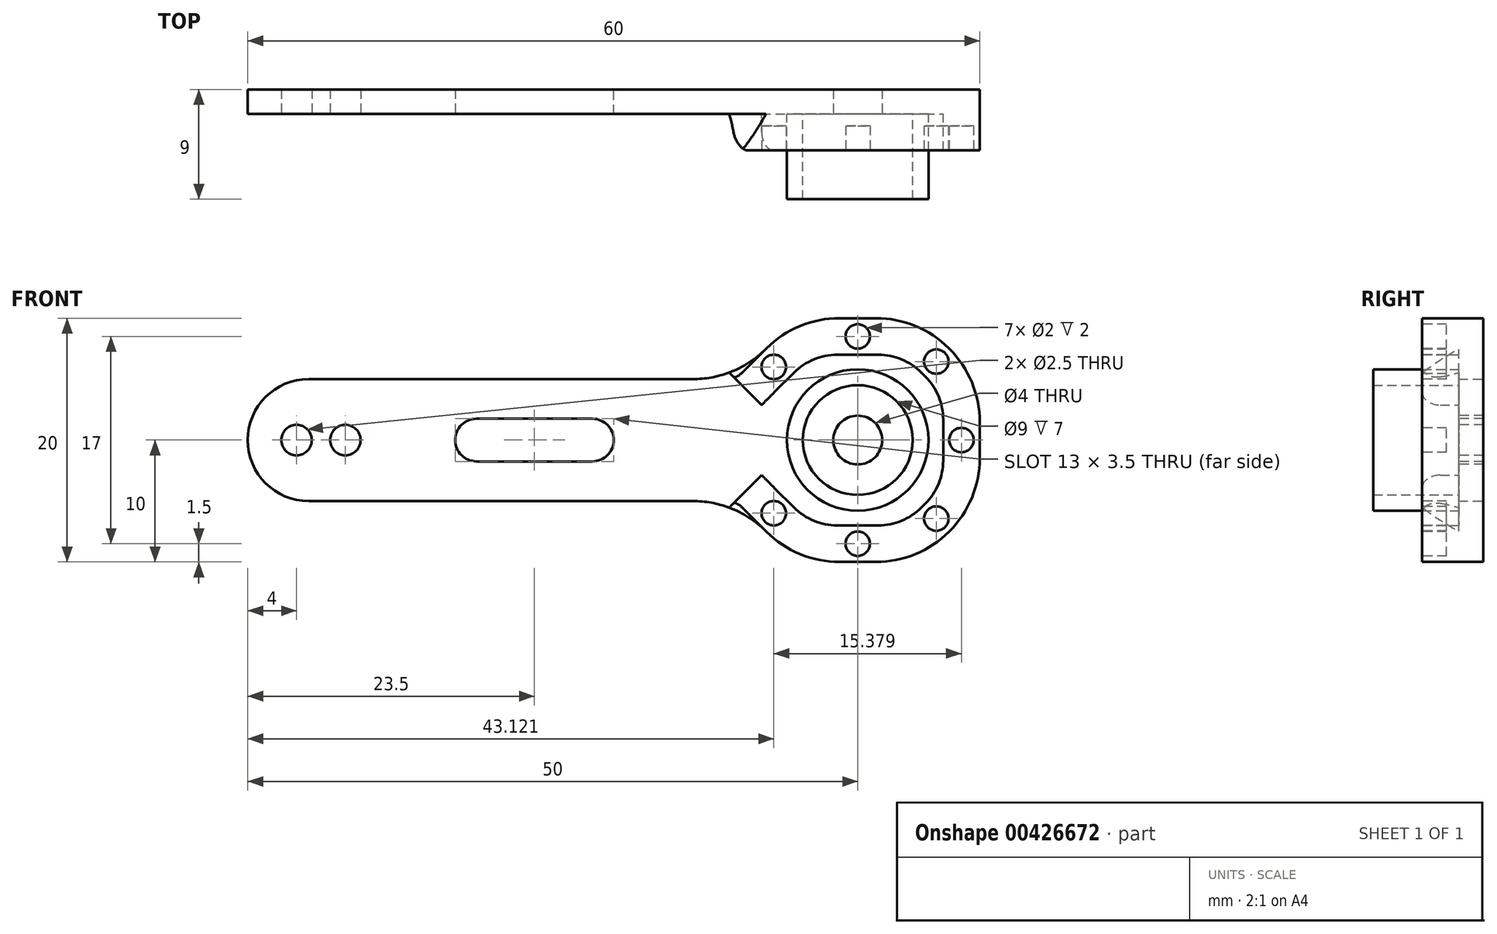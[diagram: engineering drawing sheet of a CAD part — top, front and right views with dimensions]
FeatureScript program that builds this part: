
annotation { "Feature Type Name" : "Feature", "Feature Type Description" : "" }
export const myFeature = defineFeature(function(context is Context, id is Id, definition is map)
    precondition{}
    {
        {
            var Q0;
            Q0=qCreatedBy(makeId("Front.planeOp"),FACE);
            var sketch = newSketch(context, id + "F0", { "sketchPlane" : qUnion([Q0])});
            skLineSegment(sketch, "E0", {"start": v(0, 0) * mm, "end": v(40, 0) * mm});
            skLineSegment(sketch, "E1", {"start": v(60, 0) * mm, "end": v(60, 10) * mm});
            skLineSegment(sketch, "E2", {"start": v(40, 10) * mm, "end": v(0, 10) * mm});
            skLineSegment(sketch, "E3", {"start": v(0, 10) * mm, "end": v(0, 0) * mm});
            skLineSegment(sketch, "E4", {"start": v(40, 10) * mm, "end": v(45, 15) * mm});
            skLineSegment(sketch, "E5", {"start": v(45, 15) * mm, "end": v(55, 15) * mm});
            skLineSegment(sketch, "E6", {"start": v(55, 15) * mm, "end": v(60, 10) * mm});
            skLineSegment(sketch, "E7", {"start": v(40, 0) * mm, "end": v(45, -5) * mm});
            skLineSegment(sketch, "E8", {"start": v(45, -5) * mm, "end": v(55, -5) * mm});
            skLineSegment(sketch, "E9", {"start": v(55, -5) * mm, "end": v(60, 0) * mm});
            skSolve(sketch);
        }
        {
            var Q0;
            Q0 = qSketchRegion(id + "F0", true);
            extrude(context, id + "F1", {"entities" : qUnion([Q0]), "depth" : 2 * mm, "offsetDistance" : 25 * mm});
        }
        {
            var Q0;
            Q0=makeQuery(id+"F1.opExtrude","CAP_FACE",FACE,{"disambiguationData":[OSD([sQuery(id+"F0.wireOp",EDGE,"E0"),sQuery(id+"F0.wireOp",EDGE,"E1"),sQuery(id+"F0.wireOp",EDGE,"E2"),sQuery(id+"F0.wireOp",EDGE,"E3"),sQuery(id+"F0.wireOp",EDGE,"E4"),sQuery(id+"F0.wireOp",EDGE,"E5"),sQuery(id+"F0.wireOp",EDGE,"E6"),sQuery(id+"F0.wireOp",EDGE,"E7"),sQuery(id+"F0.wireOp",EDGE,"E8"),sQuery(id+"F0.wireOp",EDGE,"E9")])],"isStart":false});
            var sketch = newSketch(context, id + "F2", { "sketchPlane" : qUnion([Q0])});
            skCircle(sketch, "E10", {"center": v(4, 5) * mm, "radius": 1.25 * mm});
            skCircle(sketch, "E11", {"center": v(8, 5) * mm, "radius": 1.25 * mm});
            skSolve(sketch);
        }
        {
            var Q0;
            Q0 = qSketchRegion(id + "F2", true);
            extrude(context, id + "F3", {"entities" : qUnion([Q0]), "operationType" : NewBodyOperationType.REMOVE, "oppositeDirection" : true, "depth" : 25 * mm, "offsetDistance" : 25 * mm});
        }
        {
            var Q0;
            Q0=makeQuery(id+"F1.opExtrude","CAP_FACE",FACE,{"disambiguationData":[OSD([sQuery(id+"F0.wireOp",EDGE,"E0"),sQuery(id+"F0.wireOp",EDGE,"E1"),sQuery(id+"F0.wireOp",EDGE,"E2"),sQuery(id+"F0.wireOp",EDGE,"E3"),sQuery(id+"F0.wireOp",EDGE,"E4"),sQuery(id+"F0.wireOp",EDGE,"E5"),sQuery(id+"F0.wireOp",EDGE,"E6"),sQuery(id+"F0.wireOp",EDGE,"E7"),sQuery(id+"F0.wireOp",EDGE,"E8"),sQuery(id+"F0.wireOp",EDGE,"E9")])],"isStart":false});
            var sketch = newSketch(context, id + "F4", { "sketchPlane" : qUnion([Q0])});
            skCircle(sketch, "E12", {"center": v(50, 5) * mm, "radius": 2 * mm});
            skSolve(sketch);
        }
        {
            var Q0;
            Q0 = qSketchRegion(id + "F4", true);
            extrude(context, id + "F5", {"entities" : qUnion([Q0]), "operationType" : NewBodyOperationType.REMOVE, "oppositeDirection" : true, "depth" : 25 * mm, "offsetDistance" : 25 * mm});
        }
        {
            var Q0;
            Q0=makeQuery(id+"F1.opExtrude","CAP_FACE",FACE,{"disambiguationData":[OSD([sQuery(id+"F0.wireOp",EDGE,"E0"),sQuery(id+"F0.wireOp",EDGE,"E1"),sQuery(id+"F0.wireOp",EDGE,"E2"),sQuery(id+"F0.wireOp",EDGE,"E3"),sQuery(id+"F0.wireOp",EDGE,"E4"),sQuery(id+"F0.wireOp",EDGE,"E5"),sQuery(id+"F0.wireOp",EDGE,"E6"),sQuery(id+"F0.wireOp",EDGE,"E7"),sQuery(id+"F0.wireOp",EDGE,"E8"),sQuery(id+"F0.wireOp",EDGE,"E9")])],"isStart":false});
            var sketch = newSketch(context, id + "F6", { "sketchPlane" : qUnion([Q0])});
            skCircle(sketch, "E13", {"center": v(50, 5) * mm, "radius": 4.5 * mm});
            skCircle(sketch, "E14", {"center": v(50, 5) * mm, "radius": 5.8 * mm});
            skSolve(sketch);
        }
        {
            var Q0;
            Q0 = qSketchRegion(id + "F6", true);
            extrude(context, id + "F7", {"entities" : qUnion([Q0]), "operationType" : NewBodyOperationType.ADD, "depth" : 7 * mm, "offsetDistance" : 25 * mm});
        }
        {
            var Q0;
            {var subQ0=sQuery(id+"F0.wireOp",EDGE,"E8");var subQ1=sQuery(id+"F0.wireOp",EDGE,"E7");var subQ2=sQuery(id+"F0.wireOp",EDGE,"E6");var subQ3=sQuery(id+"F0.wireOp",EDGE,"E5");var subQ4=sQuery(id+"F0.wireOp",EDGE,"E4");var subQ5=sQuery(id+"F0.wireOp",EDGE,"E9");var subQ6=sQuery(id+"F0.wireOp",EDGE,"E0");var subQ7=sQuery(id+"F0.wireOp",EDGE,"E3");var subQ8=sQuery(id+"F0.wireOp",EDGE,"E1");var subQ9=sQuery(id+"F0.wireOp",EDGE,"E2");Q0=makeQuery(id+"F7.boolean.opBoolean","SPLIT",FACE,{"disambiguationData":[TD([makeQuery(id+"F1.opExtrude","SWEPT_FACE",FACE,{"disambiguationData":[OSD([subQ6])]})])],"derivedFrom":makeQuery(id+"F1.opExtrude","CAP_FACE",FACE,{"disambiguationData":[OSD([subQ6,subQ8,subQ9,subQ7,subQ4,subQ3,subQ2,subQ1,subQ0,subQ5])],"isStart":false})});}
            var sketch = newSketch(context, id + "F8", { "sketchPlane" : qUnion([Q0])});
            skLineSegment(sketch, "E15", {"start": v(40, 0) * mm, "end": v(45, -5) * mm});
            skLineSegment(sketch, "E16", {"start": v(45, -5) * mm, "end": v(55, -5) * mm});
            skLineSegment(sketch, "E17", {"start": v(55, -5) * mm, "end": v(60, 0) * mm});
            skLineSegment(sketch, "E18", {"start": v(60, 0) * mm, "end": v(60, 10) * mm});
            skLineSegment(sketch, "E19", {"start": v(60, 10) * mm, "end": v(55, 15) * mm});
            skLineSegment(sketch, "E20", {"start": v(55, 15) * mm, "end": v(45, 15) * mm});
            skLineSegment(sketch, "E21", {"start": v(45, 15) * mm, "end": v(40, 10) * mm});
            skLineSegment(sketch, "E22.0", {"start": v(46.24, 12) * mm, "end": v(42.12, 7.88) * mm});
            skLineSegment(sketch, "E22.1", {"start": v(53.76, 12) * mm, "end": v(46.24, 12) * mm});
            skLineSegment(sketch, "E22.2", {"start": v(57, 8.76) * mm, "end": v(53.76, 12) * mm});
            skLineSegment(sketch, "E22.3", {"start": v(42.12, 2.12) * mm, "end": v(46.24, -2) * mm});
            skLineSegment(sketch, "E22.4", {"start": v(46.24, -2) * mm, "end": v(53.76, -2) * mm});
            skLineSegment(sketch, "E22.5", {"start": v(53.76, -2) * mm, "end": v(57, 1.24) * mm});
            skLineSegment(sketch, "E22.6", {"start": v(57, 1.24) * mm, "end": v(57, 8.76) * mm});
            skLineSegment(sketch, "E23", {"start": v(42.12, 7.88) * mm, "end": v(40, 10) * mm});
            skLineSegment(sketch, "E24", {"start": v(42.12, 2.12) * mm, "end": v(40, 0) * mm});
            skLineSegment(sketch, "E25", {"start": v(53.76, 12) * mm, "end": v(55, 15) * mm});
            skLineSegment(sketch, "E26", {"start": v(53.76, -2) * mm, "end": v(55, -5) * mm});
            skSolve(sketch);
        }
        {
            var Q0;
            Q0 = qSketchRegion(id + "F8", true);
            extrude(context, id + "F9", {"entities" : qUnion([Q0]), "operationType" : NewBodyOperationType.ADD, "depth" : 3 * mm, "offsetDistance" : 25 * mm});
        }
        {
            var Q0;
            Q0=makeQuery(id+"F9.opExtrude","CAP_FACE",FACE,{"disambiguationData":[OSD([sQuery(id+"F8.wireOp",EDGE,"E15"),sQuery(id+"F8.wireOp",EDGE,"E16"),sQuery(id+"F8.wireOp",EDGE,"E17"),sQuery(id+"F8.wireOp",EDGE,"E18"),sQuery(id+"F8.wireOp",EDGE,"E19"),sQuery(id+"F8.wireOp",EDGE,"E20"),sQuery(id+"F8.wireOp",EDGE,"E21"),sQuery(id+"F8.wireOp",EDGE,"E22.0"),sQuery(id+"F8.wireOp",EDGE,"E22.1"),sQuery(id+"F8.wireOp",EDGE,"E22.2"),sQuery(id+"F8.wireOp",EDGE,"E22.3"),sQuery(id+"F8.wireOp",EDGE,"E22.4"),sQuery(id+"F8.wireOp",EDGE,"E22.5"),sQuery(id+"F8.wireOp",EDGE,"E22.6"),sQuery(id+"F8.wireOp",EDGE,"E23"),sQuery(id+"F8.wireOp",EDGE,"E24")])],"isStart":false});
            var sketch = newSketch(context, id + "F10", { "sketchPlane" : qUnion([Q0])});
            skCircle(sketch, "E27", {"center": v(50, -3.5) * mm, "radius": 1 * mm});
            skCircle(sketch, "E28", {"center": v(58.5, 5) * mm, "radius": 1 * mm});
            skPoint(sketch, "E28.centerSnap0", {"position": v(57, 5) * mm});
            skCircle(sketch, "E29", {"center": v(56.44, 11.44) * mm, "radius": 1 * mm});
            skCircle(sketch, "E30", {"center": v(50, 13.5) * mm, "radius": 1 * mm});
            skCircle(sketch, "E31", {"center": v(43.12, 11) * mm, "radius": 1 * mm});
            skCircle(sketch, "E32", {"center": v(43.12, -1) * mm, "radius": 1 * mm});
            skPoint(sketch, "E33.start.orphan", {"position": v(44.18, 0.06) * mm});
            skPoint(sketch, "E34.orphan", {"position": v(44.18, 9.94) * mm});
            skPoint(sketch, "E35.orphan", {"position": v(55.38, 10.38) * mm});
            skPoint(sketch, "E36.end.orphan", {"position": v(57.5, 12.5) * mm});
            skCircle(sketch, "E37", {"center": v(56.44, -1.44) * mm, "radius": 1 * mm});
            skPoint(sketch, "E38.orphan", {"position": v(57.5, -2.5) * mm});
            skPoint(sketch, "E39.orphan", {"position": v(55.38, -0.38) * mm});
            skSolve(sketch);
        }
        {
            var Q0;
            Q0 = qSketchRegion(id + "F10", true);
            extrude(context, id + "F11", {"entities" : qUnion([Q0]), "operationType" : NewBodyOperationType.REMOVE, "oppositeDirection" : true, "depth" : 2 * mm, "offsetDistance" : 25 * mm});
        }
        {
            var Q0;
            Q0=makeQuery(id+"F1.opExtrude","SWEPT_EDGE",EDGE,{"disambiguationData":[OSD([sQuery(id+"F0.wireOp",EDGE,"E2"),sQuery(id+"F0.wireOp",EDGE,"E4")])]});
            var Q1;
            Q1=makeQuery(id+"F9.boolean.opBoolean","MERGE",EDGE,{"derivedFrom":[makeQuery(id+"F1.opExtrude","SWEPT_EDGE",EDGE,{"disambiguationData":[OSD([sQuery(id+"F0.wireOp",EDGE,"E4"),sQuery(id+"F0.wireOp",EDGE,"E5")])]}),makeQuery(id+"F9.opExtrude","SWEPT_EDGE",EDGE,{"disambiguationData":[OSD([sQuery(id+"F8.wireOp",EDGE,"E20"),sQuery(id+"F8.wireOp",EDGE,"E21")])]})]});
            var Q2;
            Q2=makeQuery(id+"F9.boolean.opBoolean","MERGE",EDGE,{"derivedFrom":[makeQuery(id+"F1.opExtrude","SWEPT_EDGE",EDGE,{"disambiguationData":[OSD([sQuery(id+"F0.wireOp",EDGE,"E5"),sQuery(id+"F0.wireOp",EDGE,"E6")])]}),makeQuery(id+"F9.opExtrude","SWEPT_EDGE",EDGE,{"disambiguationData":[OSD([sQuery(id+"F8.wireOp",EDGE,"E19"),sQuery(id+"F8.wireOp",EDGE,"E20")])]})]});
            var Q3;
            Q3=makeQuery(id+"F9.boolean.opBoolean","MERGE",EDGE,{"derivedFrom":[makeQuery(id+"F1.opExtrude","SWEPT_EDGE",EDGE,{"disambiguationData":[OSD([sQuery(id+"F0.wireOp",EDGE,"E1"),sQuery(id+"F0.wireOp",EDGE,"E6")])]}),makeQuery(id+"F9.opExtrude","SWEPT_EDGE",EDGE,{"disambiguationData":[OSD([sQuery(id+"F8.wireOp",EDGE,"E18"),sQuery(id+"F8.wireOp",EDGE,"E19")])]})]});
            var Q4;
            Q4=makeQuery(id+"F9.boolean.opBoolean","MERGE",EDGE,{"derivedFrom":[makeQuery(id+"F1.opExtrude","SWEPT_EDGE",EDGE,{"disambiguationData":[OSD([sQuery(id+"F0.wireOp",EDGE,"E1"),sQuery(id+"F0.wireOp",EDGE,"E9")])]}),makeQuery(id+"F9.opExtrude","SWEPT_EDGE",EDGE,{"disambiguationData":[OSD([sQuery(id+"F8.wireOp",EDGE,"E17"),sQuery(id+"F8.wireOp",EDGE,"E18")])]})]});
            var Q5;
            Q5=makeQuery(id+"F9.boolean.opBoolean","MERGE",EDGE,{"derivedFrom":[makeQuery(id+"F1.opExtrude","SWEPT_EDGE",EDGE,{"disambiguationData":[OSD([sQuery(id+"F0.wireOp",EDGE,"E8"),sQuery(id+"F0.wireOp",EDGE,"E9")])]}),makeQuery(id+"F9.opExtrude","SWEPT_EDGE",EDGE,{"disambiguationData":[OSD([sQuery(id+"F8.wireOp",EDGE,"E16"),sQuery(id+"F8.wireOp",EDGE,"E17")])]})]});
            var Q6;
            Q6=makeQuery(id+"F9.boolean.opBoolean","MERGE",EDGE,{"derivedFrom":[makeQuery(id+"F1.opExtrude","SWEPT_EDGE",EDGE,{"disambiguationData":[OSD([sQuery(id+"F0.wireOp",EDGE,"E7"),sQuery(id+"F0.wireOp",EDGE,"E8")])]}),makeQuery(id+"F9.opExtrude","SWEPT_EDGE",EDGE,{"disambiguationData":[OSD([sQuery(id+"F8.wireOp",EDGE,"E15"),sQuery(id+"F8.wireOp",EDGE,"E16")])]})]});
            var Q7;
            Q7=makeQuery(id+"F1.opExtrude","SWEPT_EDGE",EDGE,{"disambiguationData":[OSD([sQuery(id+"F0.wireOp",EDGE,"E0"),sQuery(id+"F0.wireOp",EDGE,"E7")])]});
            fillet(context, id + "F12", {"entities" : qUnion([Q0, Q1, Q2, Q3, Q4, Q5, Q6, Q7]), "radius" : 8.5 * mm, "tangentPropagation" : true, "allowEdgeOverflow" : false});
        }
        {
            var Q0;
            Q0=makeQuery(id+"F9.opExtrude","SWEPT_EDGE",EDGE,{"disambiguationData":[OSD([sQuery(id+"F8.wireOp",EDGE,"E22.4"),sQuery(id+"F8.wireOp",EDGE,"E22.5")])]});
            var Q1;
            Q1=makeQuery(id+"F9.opExtrude","SWEPT_EDGE",EDGE,{"disambiguationData":[OSD([sQuery(id+"F8.wireOp",EDGE,"E22.5"),sQuery(id+"F8.wireOp",EDGE,"E22.6")])]});
            var Q2;
            Q2=makeQuery(id+"F9.opExtrude","SWEPT_EDGE",EDGE,{"disambiguationData":[OSD([sQuery(id+"F8.wireOp",EDGE,"E22.2"),sQuery(id+"F8.wireOp",EDGE,"E22.6")])]});
            var Q3;
            Q3=makeQuery(id+"F9.opExtrude","SWEPT_EDGE",EDGE,{"disambiguationData":[OSD([sQuery(id+"F8.wireOp",EDGE,"E22.1"),sQuery(id+"F8.wireOp",EDGE,"E22.2")])]});
            var Q4;
            Q4=makeQuery(id+"F9.opExtrude","SWEPT_EDGE",EDGE,{"disambiguationData":[OSD([sQuery(id+"F8.wireOp",EDGE,"E22.0"),sQuery(id+"F8.wireOp",EDGE,"E22.1")])]});
            var Q5;
            Q5=makeQuery(id+"F9.opExtrude","SWEPT_EDGE",EDGE,{"disambiguationData":[OSD([sQuery(id+"F8.wireOp",EDGE,"E22.3"),sQuery(id+"F8.wireOp",EDGE,"E22.4")])]});
            var Q6;
            {var subQ0=sQuery(id+"F0.wireOp",EDGE,"E2");Q6=makeQuery(id+"F12.opFillet","TWEAK_EDGE",EDGE,{"derivedFrom":[makeQuery(id+"F9.boolean.opBoolean","MERGE",VERTEX,{"derivedFrom":[makeQuery(id+"F1.opExtrude","CAP_VERTEX",VERTEX,{"disambiguationData":[OSD([subQ0,sQuery(id+"F0.wireOp",EDGE,"E4")])],"isStart":false}),makeQuery(id+"F9.opExtrude","CAP_VERTEX",VERTEX,{"disambiguationData":[OSD([subQ0,sQuery(id+"F8.wireOp",EDGE,"E21"),sQuery(id+"F8.wireOp",EDGE,"E23")])],"isStart":true})]})]});}
            fillet(context, id + "F13", {"entities" : qUnion([Q0, Q1, Q2, Q3, Q4, Q5, Q6]), "radius" : 5 * mm, "tangentPropagation" : true, "allowEdgeOverflow" : false});
        }
        {
            var Q0;
            {var subQ0=sQuery(id+"F0.wireOp",EDGE,"E0");Q0=makeQuery(id+"F12.opFillet","TWEAK_EDGE",EDGE,{"derivedFrom":[makeQuery(id+"F9.boolean.opBoolean","MERGE",VERTEX,{"derivedFrom":[makeQuery(id+"F1.opExtrude","CAP_VERTEX",VERTEX,{"disambiguationData":[OSD([subQ0,sQuery(id+"F0.wireOp",EDGE,"E7")])],"isStart":false}),makeQuery(id+"F9.opExtrude","CAP_VERTEX",VERTEX,{"disambiguationData":[OSD([subQ0,sQuery(id+"F8.wireOp",EDGE,"E15"),sQuery(id+"F8.wireOp",EDGE,"E24")])],"isStart":true})]})]});}
            fillet(context, id + "F14", {"entities" : qUnion([Q0]), "radius" : 5 * mm, "tangentPropagation" : true, "allowEdgeOverflow" : false});
        }
        {
            var Q0;
            Q0=makeQuery(id+"F9.opExtrude","CAP_EDGE",EDGE,{"disambiguationData":[OSD([sQuery(id+"F8.wireOp",EDGE,"E24")])],"isStart":true});
            var Q1;
            Q1=makeQuery(id+"F9.opExtrude","CAP_EDGE",EDGE,{"disambiguationData":[OSD([sQuery(id+"F8.wireOp",EDGE,"E23")])],"isStart":true});
            var Q2;
            Q2=makeQuery(id+"F9.opExtrude","CAP_EDGE",EDGE,{"disambiguationData":[OSD([sQuery(id+"F8.wireOp",EDGE,"E24")])],"isStart":false});
            var Q3;
            Q3=makeQuery(id+"F9.opExtrude","CAP_EDGE",EDGE,{"disambiguationData":[OSD([sQuery(id+"F8.wireOp",EDGE,"E23")])],"isStart":false});
            fillet(context, id + "F15", {"entities" : qUnion([Q0, Q1, Q2, Q3]), "radius" : 1.5 * mm, "tangentPropagation" : true, "allowEdgeOverflow" : false});
        }
        {
            var Q0;
            Q0=makeQuery(id+"F1.opExtrude","SWEPT_EDGE",EDGE,{"disambiguationData":[OSD([sQuery(id+"F0.wireOp",EDGE,"E0"),sQuery(id+"F0.wireOp",EDGE,"E3")])]});
            var Q1;
            Q1=makeQuery(id+"F1.opExtrude","SWEPT_EDGE",EDGE,{"disambiguationData":[OSD([sQuery(id+"F0.wireOp",EDGE,"E2"),sQuery(id+"F0.wireOp",EDGE,"E3")])]});
            fillet(context, id + "F16", {"entities" : qUnion([Q0, Q1]), "radius" : 5 * mm, "tangentPropagation" : true, "allowEdgeOverflow" : false});
        }
        {
            var Q0;
            {var subQ0=sQuery(id+"F0.wireOp",EDGE,"E8");var subQ1=sQuery(id+"F0.wireOp",EDGE,"E7");var subQ2=sQuery(id+"F0.wireOp",EDGE,"E6");var subQ3=sQuery(id+"F0.wireOp",EDGE,"E5");var subQ4=sQuery(id+"F0.wireOp",EDGE,"E4");var subQ5=sQuery(id+"F0.wireOp",EDGE,"E9");var subQ6=sQuery(id+"F0.wireOp",EDGE,"E0");var subQ7=sQuery(id+"F0.wireOp",EDGE,"E3");var subQ8=sQuery(id+"F0.wireOp",EDGE,"E1");var subQ9=sQuery(id+"F0.wireOp",EDGE,"E2");Q0=makeQuery(id+"F7.boolean.opBoolean","SPLIT",FACE,{"disambiguationData":[TD([makeQuery(id+"F1.opExtrude","SWEPT_FACE",FACE,{"disambiguationData":[OSD([subQ6])]})])],"derivedFrom":makeQuery(id+"F1.opExtrude","CAP_FACE",FACE,{"disambiguationData":[OSD([subQ6,subQ8,subQ9,subQ7,subQ4,subQ3,subQ2,subQ1,subQ0,subQ5])],"isStart":false})});}
            var sketch = newSketch(context, id + "F17", { "sketchPlane" : qUnion([Q0])});
            skLineSegment(sketch, "E40.bottom", {"start": v(17, 6.75) * mm, "end": v(30, 6.75) * mm});
            skLineSegment(sketch, "E40.top", {"start": v(17, 3.25) * mm, "end": v(30, 3.25) * mm});
            skLineSegment(sketch, "E40.left", {"start": v(17, 6.75) * mm, "end": v(17, 3.25) * mm});
            skLineSegment(sketch, "E40.right", {"start": v(30, 6.75) * mm, "end": v(30, 3.25) * mm});
            skSolve(sketch);
        }
        {
            var Q0;
            Q0 = qSketchRegion(id + "F17", true);
            extrude(context, id + "F18", {"entities" : qUnion([Q0]), "operationType" : NewBodyOperationType.REMOVE, "oppositeDirection" : true, "depth" : 25 * mm, "offsetDistance" : 25 * mm});
        }
        {
            var Q0;
            Q0=makeQuery(id+"F18.boolean.opBoolean","COPY",EDGE,{"derivedFrom":makeQuery(id+"F18.opExtrude","SWEPT_EDGE",EDGE,{"disambiguationData":[OSD([sQuery(id+"F17.wireOp",EDGE,"E40.bottom"),sQuery(id+"F17.wireOp",EDGE,"E40.left")])]})});
            var Q1;
            Q1=makeQuery(id+"F18.boolean.opBoolean","COPY",EDGE,{"derivedFrom":makeQuery(id+"F18.opExtrude","SWEPT_EDGE",EDGE,{"disambiguationData":[OSD([sQuery(id+"F17.wireOp",EDGE,"E40.bottom"),sQuery(id+"F17.wireOp",EDGE,"E40.right")])]})});
            var Q2;
            Q2=makeQuery(id+"F18.boolean.opBoolean","COPY",EDGE,{"derivedFrom":makeQuery(id+"F18.opExtrude","SWEPT_EDGE",EDGE,{"disambiguationData":[OSD([sQuery(id+"F17.wireOp",EDGE,"E40.top"),sQuery(id+"F17.wireOp",EDGE,"E40.right")])]})});
            var Q3;
            Q3=makeQuery(id+"F18.boolean.opBoolean","COPY",EDGE,{"derivedFrom":makeQuery(id+"F18.opExtrude","SWEPT_EDGE",EDGE,{"disambiguationData":[OSD([sQuery(id+"F17.wireOp",EDGE,"E40.top"),sQuery(id+"F17.wireOp",EDGE,"E40.left")])]})});
            fillet(context, id + "F19", {"entities" : qUnion([Q0, Q1, Q2, Q3]), "radius" : 1.75 * mm, "tangentPropagation" : true, "allowEdgeOverflow" : false});
        }
    });
